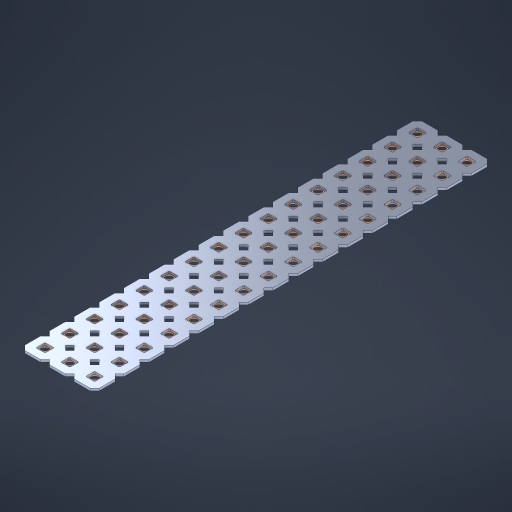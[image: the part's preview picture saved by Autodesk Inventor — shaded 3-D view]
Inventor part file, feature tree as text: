
AUTODESK INVENTOR PART (.ipt)
format: ipt  version: 2023 (Build 270158000, 158)  size: 814,592 bytes
history: native  units: in
note: dims shown in document units (in); Inventor stores cm internally (conversion verified against a paired STEP export)
features: other x49, extrude x47, sketch x2, pattern_linear x1
ambient origin geometry x8: Origin, YZ Plane, XZ Plane, XY Plane, X Axis, Y Axis, Z Axis, Center Point
bodies: Solid1 (feature_tree), Body (feature_tree)
feature tree (99):
  pattern_linear  "Rectangular Pattern1"  Spacing1=0.09in  [1 undecoded]
  sketch  "Sketch1"  dims[d1=0.5in]
  sketch  "Sketch2"  dims[d2=0.182in d3=0.09in d4=0.09in d5=0.09in d6=0.09in d7=0.09in d8=0.09in d9=0.09in d10=0.09in d11=0.02in d13=0.0in d14=0.172in d15=0.0625in d16=0.0in d19=0.5in d22=0.5in]
  other  "Srf1"
  other  "Srf126"
  other  "Srf127"
  other  "Srf128"
  other  "Srf129"
  other  "Srf130"
  other  "Srf131"
  other  "Srf250"
  other  "Srf251"
  other  "Srf252"
  other  "Srf253"
  other  "Srf254"
  other  "Srf255"
  other  "Srf256"
  other  "Srf257"
  other  "Srf258"
  other  "Srf268"
  other  "Srf269"
  other  "Srf270"
  other  "Srf271"
  other  "Srf272"
  other  "Srf273"
  other  "Srf274"
  other  "Srf275"
  other  "Srf276"
  other  "Srf277"
  other  "Srf278"
  other  "Srf279"
  other  "Srf280"
  other  "Srf281"
  other  "Srf282"
  other  "Srf283"
  other  "Srf293"
  other  "Srf294"
  other  "Srf295"
  other  "Srf296"
  other  "Srf297"
  other  "Srf298"
  other  "Srf299"
  other  "Srf300"
  other  "Srf301"
  other  "Srf302"
  other  "Srf303"
  other  "Srf304"
  other  "Srf305"
  other  "Srf306"
  other  "Srf307"
  other  "Srf308"
  other  "Circle"
  extrude  "ExtrusionSrf126"  Depth=0.09in
  extrude  "ExtrusionSrf127"  Depth=0.09in
  extrude  "ExtrusionSrf128"  Depth=0.09in
  extrude  "ExtrusionSrf129"  Depth=0.09in
  extrude  "ExtrusionSrf130"  Depth=0.09in
  extrude  "ExtrusionSrf131"  Depth=0.09in
  extrude  "ExtrusionSrf250"  Depth=0.09in
  extrude  "ExtrusionSrf251"  Depth=0.02in
  extrude  "ExtrusionSrf252"  TaperAngle=0.0deg  [1 undecoded]
  extrude  "ExtrusionSrf253"  Depth=0.5in
  extrude  "ExtrusionSrf254"  Depth=0.5in TaperAngle=0.0deg
  extrude  "ExtrusionSrf255"  Depth=0.5in
  extrude  "ExtrusionSrf256"  Depth=0.5in
  extrude  "ExtrusionSrf257"  [1 undecoded]
  extrude  "ExtrusionSrf258"  [1 undecoded]
  extrude  "ExtrusionSrf268"  [1 undecoded]
  extrude  "ExtrusionSrf269"  [1 undecoded]
  extrude  "ExtrusionSrf270"  [1 undecoded]
  extrude  "ExtrusionSrf271"  [1 undecoded]
  extrude  "ExtrusionSrf272"  [1 undecoded]
  extrude  "ExtrusionSrf273"  [1 undecoded]
  extrude  "ExtrusionSrf274"  [1 undecoded]
  extrude  "ExtrusionSrf275"  [1 undecoded]
  extrude  "ExtrusionSrf276"  [1 undecoded]
  extrude  "ExtrusionSrf277"  [1 undecoded]
  extrude  "ExtrusionSrf278"  [1 undecoded]
  extrude  "ExtrusionSrf279"  [1 undecoded]
  extrude  "ExtrusionSrf280"  [1 undecoded]
  extrude  "ExtrusionSrf281"  [1 undecoded]
  extrude  "ExtrusionSrf282"  [1 undecoded]
  extrude  "ExtrusionSrf283"  [1 undecoded]
  extrude  "ExtrusionSrf293"  [1 undecoded]
  extrude  "ExtrusionSrf294"  [1 undecoded]
  extrude  "ExtrusionSrf295"  [1 undecoded]
  extrude  "ExtrusionSrf296"  [1 undecoded]
  extrude  "ExtrusionSrf297"  [1 undecoded]
  extrude  "ExtrusionSrf298"  [1 undecoded]
  extrude  "ExtrusionSrf299"  [1 undecoded]
  extrude  "ExtrusionSrf300"  [1 undecoded]
  extrude  "ExtrusionSrf301"  [1 undecoded]
  extrude  "ExtrusionSrf302"  [1 undecoded]
  extrude  "ExtrusionSrf303"  [1 undecoded]
  extrude  "ExtrusionSrf304"  [1 undecoded]
  extrude  "ExtrusionSrf305"  [1 undecoded]
  extrude  "ExtrusionSrf306"  [1 undecoded]
  extrude  "ExtrusionSrf307"  [1 undecoded]
  extrude  "ExtrusionSrf308"  [1 undecoded]
note: 36 required parameter values undecoded (feature->parameter linkage not recoverable at this tier; creation-order binding heuristic only, values carry confidence <= 0.55)
